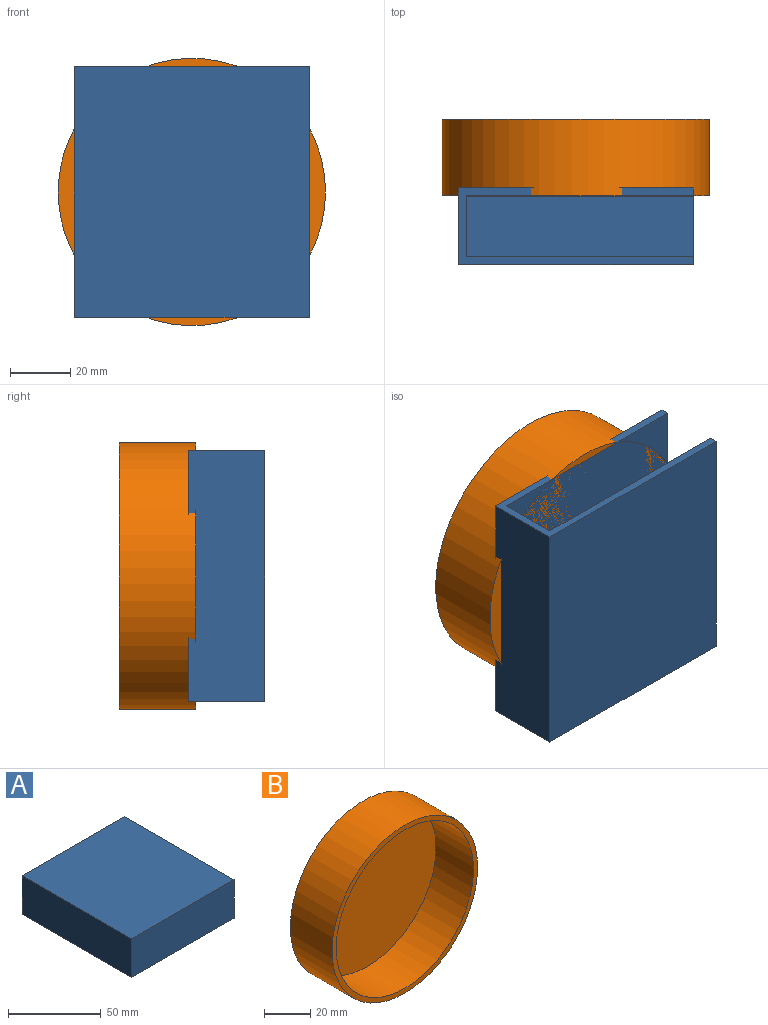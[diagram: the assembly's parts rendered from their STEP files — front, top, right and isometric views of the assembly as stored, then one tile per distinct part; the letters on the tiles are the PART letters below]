
ASSEMBLY  parts=2 mates=1
PART A: 10 faces, bbox 78x83.3x25.4 mm
  f0: plane 78.02x25.4mm, normal (0,1,0), area 447.9mm2, adj f1,f3,f4,f5,f7,f8,f9
  f1: plane 83.33x25.4mm, normal (1,0,0), area 474.9mm2, adj f0,f2,f4,f5,f6,f8,f9
  f2: plane 78.02x25.4mm, normal (0,-1,0), area 1981.7mm2, adj f1,f3,f4,f5
  f3: plane 83.33x25.4mm, normal (-1,0,0), area 2116.6mm2, adj f0,f2,f4,f5
  f4: plane 83.33x78.02mm, normal (0,0,1), area 6501.2mm2, adj f0,f1,f2,f3
  f5: plane 83.33x78.02mm, normal (0,0,-1), area 6501.2mm2, adj f0,f1,f2,f3
  f6: plane 75.48x20.32mm, normal (0,1,0), area 1533.7mm2, adj f1,f7,f8,f9
  f7: plane 80.79x20.32mm, normal (1,0,0), area 1641.6mm2, adj f0,f6,f8,f9
  f8: plane 80.79x75.48mm, normal (0,0,-1), area 6097.9mm2, adj f0,f1,f6,f7
  f9: plane 80.79x75.48mm, normal (0,0,1), area 6097.9mm2, adj f0,f1,f6,f7
PART B: 5 faces, bbox 88.8x25.4x88.8 mm
  f0: cylinder r=44.38mm len=88.76mm, axis (0,1,0), area 7083mm2, adj f1,f2
  f1: plane 88.76x88.76mm, normal (0,-1,0), area 688mm2, adj f0,f3
  f2: plane 88.76x88.76mm, normal (0,1,0), area 6188.1mm2, adj f0
  f3: cylinder r=41.84mm len=83.68mm, axis (0,1,0), area 6009.9mm2, adj f1,f4
  f4: plane 83.68x83.68mm, normal (0,-1,0), area 5500.1mm2, adj f3
PLACE A rot(axis=(1,0,0),90deg) t=(63.46,25.4,25.13)mm
PLACE B rot(axis=(0.71,0,-0.71),180deg) t=(39.01,22.86,41.66)mm
MATE fastened A.f5 <-> B.f0  axis (0,1,0) through (39.01,25.4,41.66)mm
